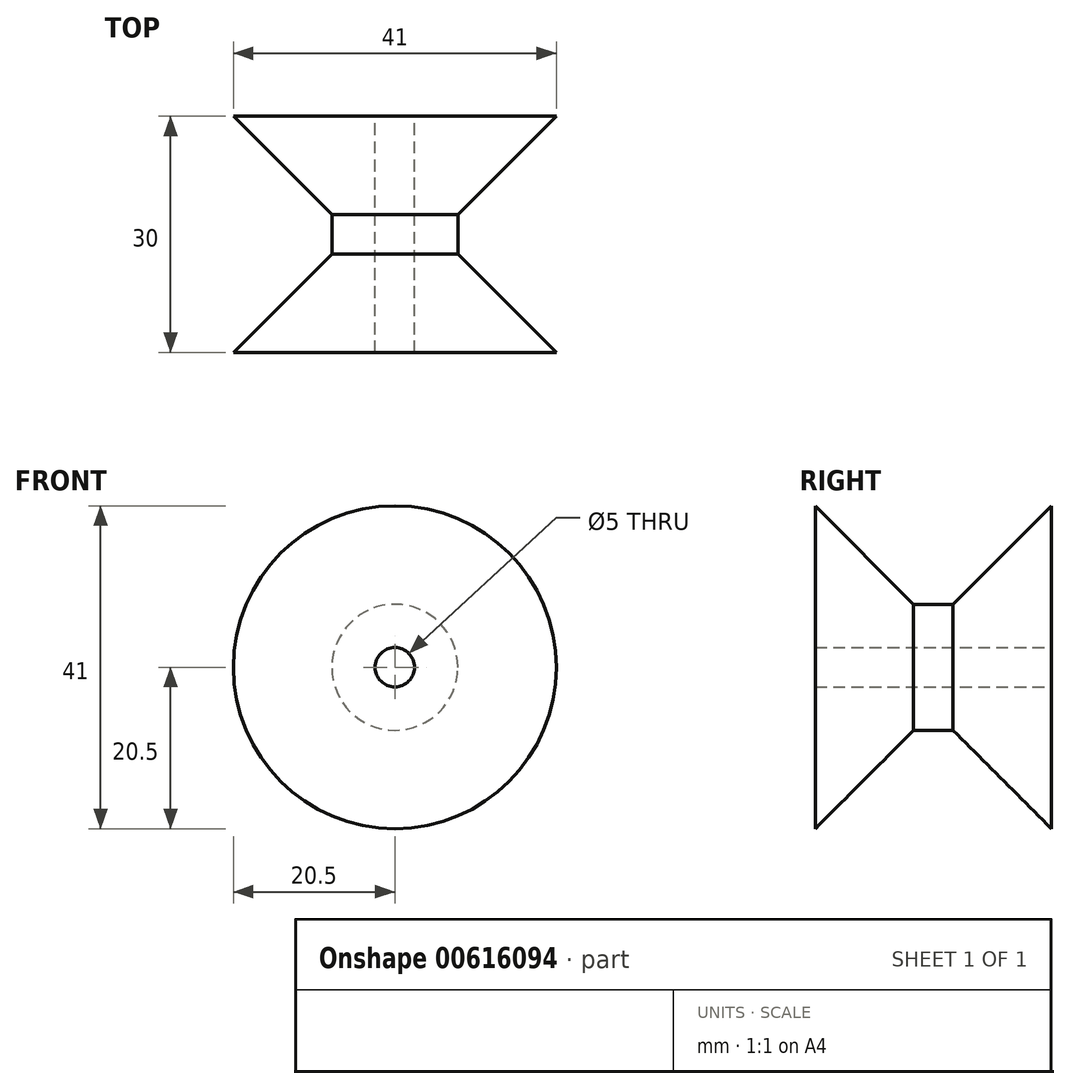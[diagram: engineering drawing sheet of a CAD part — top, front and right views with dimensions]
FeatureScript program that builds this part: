
annotation { "Feature Type Name" : "Feature", "Feature Type Description" : "" }
export const myFeature = defineFeature(function(context is Context, id is Id, definition is map)
    precondition{}
    {
        {
            var Q0;
            Q0=qCreatedBy(makeId("Top.planeOp"),FACE);
            var sketch = newSketch(context, id + "F0", { "sketchPlane" : qUnion([Q0])});
            skLineSegment(sketch, "E0", {"start": v(0, 0) * mm, "end": v(0, 30) * mm});
            skLineSegment(sketch, "E1", {"start": v(0, 30) * mm, "end": v(-20.5, 30) * mm});
            skLineSegment(sketch, "E2", {"start": v(-20.5, 30) * mm, "end": v(-8, 17.5) * mm});
            skLineSegment(sketch, "E3", {"start": v(-8, 17.5) * mm, "end": v(-8, 12.5) * mm});
            skLineSegment(sketch, "E4", {"start": v(-8, 12.5) * mm, "end": v(-20.5, 0) * mm});
            skLineSegment(sketch, "E5", {"start": v(-20.5, 0) * mm, "end": v(0, 0) * mm});
            skSolve(sketch);
        }
        {
            var Q0;
            Q0 = qSketchRegion(id + "F0", true);
            var Q1;
            Q1=sQuery(id+"F0.wireOp",EDGE,"E0");
            revolve(context, id + "F1", {"entities" : qUnion([Q0]), "axis" : qUnion([Q1]), "revolveType" : RevolveType.FULL});
        }
        {
            var Q0;
            Q0=makeQuery(id+"F1.opRevolve","SWEPT_FACE",FACE,{"disambiguationData":[OSD([sQuery(id+"F0.wireOp",EDGE,"E1")])]});
            var sketch = newSketch(context, id + "F2", { "sketchPlane" : qUnion([Q0])});
            skCircle(sketch, "E6", {"center": v(0, 0) * mm, "radius": 2.5 * mm});
            skSolve(sketch);
        }
        {
            var Q0;
            Q0 = qSketchRegion(id + "F2", true);
            extrude(context, id + "F3", {"entities" : qUnion([Q0]), "operationType" : NewBodyOperationType.REMOVE, "endBound" : BoundingType.UP_TO_NEXT, "oppositeDirection" : true, "depth" : 25 * mm, "offsetDistance" : 25 * mm});
        }
    });
